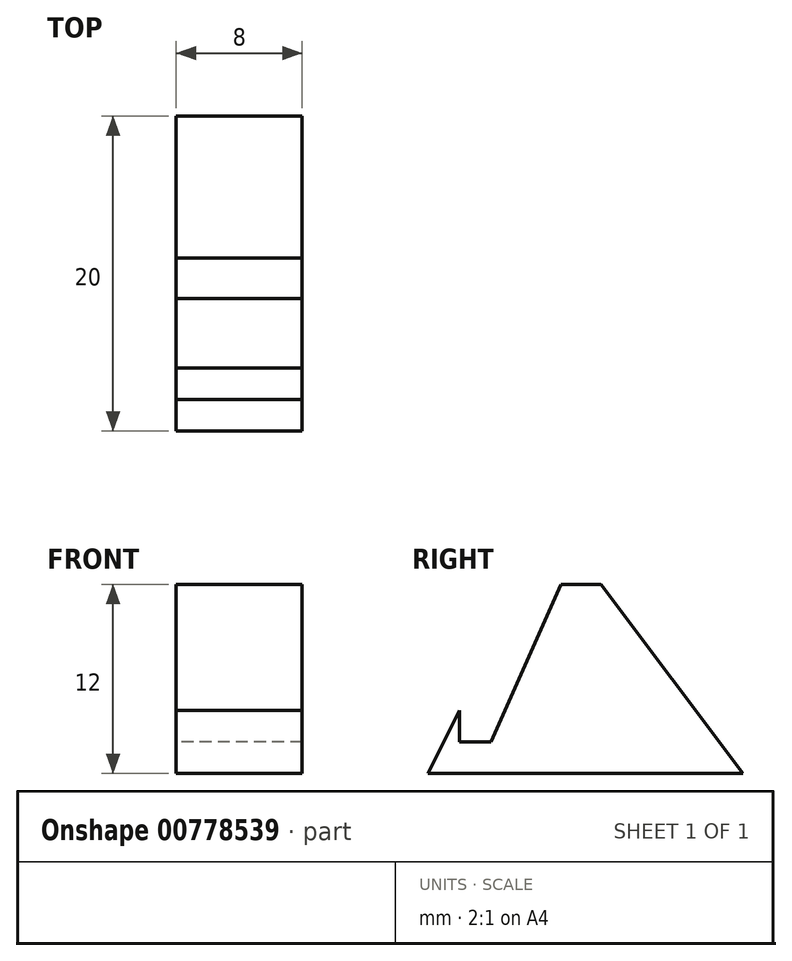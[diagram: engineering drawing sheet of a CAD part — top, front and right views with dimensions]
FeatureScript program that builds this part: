
annotation { "Feature Type Name" : "Feature", "Feature Type Description" : "" }
export const myFeature = defineFeature(function(context is Context, id is Id, definition is map)
    precondition{}
    {
        {
            var Q0;
            Q0=qCreatedBy(makeId("Right.planeOp"),FACE);
            var sketch = newSketch(context, id + "F0", { "sketchPlane" : qUnion([Q0])});
            skLineSegment(sketch, "E0", {"start": v(0, 0) * mm, "end": v(2, 4) * mm});
            skLineSegment(sketch, "E1", {"start": v(2, 4) * mm, "end": v(2, 2) * mm});
            skLineSegment(sketch, "E2", {"start": v(2, 2) * mm, "end": v(4, 2) * mm});
            skLineSegment(sketch, "E3", {"start": v(4, 2) * mm, "end": v(8.43, 12) * mm});
            skLineSegment(sketch, "E4", {"start": v(8.43, 12) * mm, "end": v(10.98, 12) * mm});
            skLineSegment(sketch, "E5", {"start": v(20, 0) * mm, "end": v(0, 0) * mm});
            skLineSegment(sketch, "E6", {"start": v(10.98, 12) * mm, "end": v(20, 0) * mm});
            skSolve(sketch);
        }
        {
            var Q0;
            Q0=makeQuery(id+"F0.imprint","IMPRINT",FACE,{"disambiguationData":[TD([[makeQuery(id+"F0.imprint","IMPRINT",EDGE,{"derivedFrom":sQuery(id+"F0.wireOp",EDGE,"E0")}),-1.0]])]});
            extrude(context, id + "F1", {"entities" : qUnion([Q0]), "depth" : 8 * mm, "offsetDistance" : 25 * mm});
        }
    });
